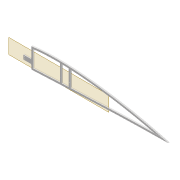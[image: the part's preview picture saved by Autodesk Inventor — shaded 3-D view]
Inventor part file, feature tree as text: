
AUTODESK INVENTOR PART (.ipt)
format: ipt  version: 2022 (Build 260153000, 153)  size: 422,912 bytes
history: native  units: mm
features: extrude x9, sketch x7, projected_geometry x5, fillet x2, shell x1, plane x1
ambient origin geometry x8: Origin, YZ Plane, XZ Plane, XY Plane, X Axis, Y Axis, Z Axis, Center Point
bodies: Solid1 (feature_tree)
feature tree (25):
  extrude  "Extrusion1"  Depth=5.0mm
  shell  "Shell1"  Thickness=2.0mm
  extrude  "Extrusion8"  Depth=5.9mm
  extrude  "Extrusion3"  Depth=10.0mm TaperAngle=0.0deg
  extrude  "Extrusion4"  Depth=2.0mm
  fillet  "Fillet1"  Radius=5.0mm
  sketch  "Sketch10"  dims[d22=4.0mm d23=0.0mm d31=2.0mm d32=5.0mm]
  extrude  "Extrusion5"  Depth=2.5mm
  plane  "Work Plane2"
  extrude  "Extrusion9"  Depth=1.6mm
  extrude  "Extrusion10"  Depth=0.5mm
  fillet  "Fillet2"  Radius=6.0mm
  extrude  "Extrusion11"  Depth=0.5mm TaperAngle=0.0deg
  extrude  "Extrusion12"  Depth=0.5mm
  sketch  "Sketch3"  dims[d0=4.0mm d1=0.0mm d2=5.0mm d7=2.0mm]
  sketch  "Sketch8"  dims[d8=2.0mm d9=5.9mm]
  sketch  "Sketch9"  dims[d13=10.0mm d14=0.0mm d16=10.0mm d17=0.0mm]
  projected_geometry  "Projected Loop4"
  projected_geometry  "Projected Loop10"
  sketch  "Sketch24"  dims[d34=1.6mm d35=2.5mm]
  projected_geometry  "Projected Loop11"
  projected_geometry  "Projected Loop12"
  sketch  "Sketch26"  dims[d37=5.0mm d38=1.6mm]
  projected_geometry  "Projected Loop13"
  sketch  "Sketch27"  dims[d40=2.5mm d62=80.0mm d63=6.0mm d64=4.0mm d65=0.0mm d66=3.0mm d67=12.0mm d68=5.0mm d69=22.0mm d70=12.0mm d71=3.05mm d72=4.0mm d73=0.0mm d74=10.0mm d75=0.0mm d76=2.0mm d77=100.0mm d78=20.0mm d79=0.5mm d80=10.0mm d81=0.0mm d82=10.0mm d83=0.0mm]
